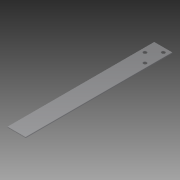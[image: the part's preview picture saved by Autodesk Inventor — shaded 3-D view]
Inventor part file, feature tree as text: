
AUTODESK INVENTOR PART (.ipt)
format: ipt  version: 2014 SP1 (Build 180222100, 222)  size: 111,616 bytes
history: native  units: in
note: dims shown in document units (in); Inventor stores cm internally (conversion verified against a paired STEP export)
features: extrude x2, sketch x2, fillet x1
ambient origin geometry x8: Origin, YZ Plane, XZ Plane, XY Plane, X Axis, Y Axis, Z Axis, Center Point
bodies: Solid1 (feature_tree)
feature tree (5):
  extrude  "Extrusion1"  Depth=8.0in
  extrude  "Extrusion2"  Depth=0.02in
  fillet  "Fillet1"  Radius=0.25in
  sketch  "Sketch1"  dims[d0=1.0in d1=8.0in]
  sketch  "Sketch2"  dims[d2=0.0625in d3=0.0in d4=0.175in d5=0.25in d6=0.25in d7=1.1811in d9=0.5in d10=0.7874in d12=0.5in d15=0.0625in d16=0.0in d17=0.02in]
